# Revit family: 353_Yard Drain Kit PVK 670_200-160
name_source: partatom
category: Plumbing Fixtures
units: mm (PartAtom-declared; Revit-internal decimal feet)

## family parameters
Always vertical = Yes
Cut with Voids When Loaded = No
Part Type = Normal
Room Calculation Point = No
Round Connector Dimension = Use Diameter
Shared = No
Work Plane-Based = No

## types (1)
- Yard drain kit 670/200-160, 40tn p/n 086317
    BD = 670 mm  [stored 2.19816 ft]
    BD1 = 389 mm
    BD2 = 317 mm  [stored 1.04003 ft]
    BD3 = 509 mm
    CAT0 = Yes
    CD = 20 mm  [stored 0.0656168 ft]
    CE = Yes
    CLBTZ = 0 mm  [stored 0 ft]
    CL_Location_5000 = 5000 mm  [stored 16.4042 ft]
    CX = 520 mm  [stored 1.70604 ft]
    CX1 = 65 mm  [stored 0.213255 ft]
    CX12 = 195 mm
    CX12__ve = -195 mm
    CX1__ve = -65 mm  [stored -0.213255 ft]
    CX2 = 259 mm
    CX22 = 130 mm
    CXX = 364 mm  [stored 1.19423 ft]
    CXX__ve = -364 mm  [stored -1.19423 ft]
    CY = 259 mm
    CY__ve = -259 mm
    D = 200 mm
    D1 = 160 mm
    D11 = No
    D116 = Yes
    D16 = No
    D20 = Yes
    DL1 = No
    DL2 = No
    DL3 = No
    Description = Yard drain chamber kit 670/200-160, 40tn p/n:086317
    H2 = 360 mm  [stored 1.1811 ft]
    MC Product Code = Yard drain kit 670/200-160, 40tn p/n:086317
    Manufacturer = Pipelife
    QmdConnectorList = 651;D;652;D1;653;D1;654;D1
    R = 100 mm  [stored 0.328084 ft]
    R1 = 80 mm  [stored 0.262467 ft]
    R2 = 80 mm  [stored 0.262467 ft]
    SW11 = No
    URL = http://www.pipelife.fi
    ZZ = 10 mm  [stored 0.0328084 ft]
    ZZ__ve = -10 mm  [stored -0.0328084 ft]
    magiPartTypeId = 353
    magiProductFamilyId = Yard Drain Kit PVK 670/200-160
    magiProductId = Yard Drain Kit PVK 670/200-160

note: [stored X ft] marks values corroborated as IEEE doubles in the binary element streams (Revit-internal decimal feet)

## geometry (parser evidence)
native form markers: Sweep x2
no freeform markers — native parametric forms only
